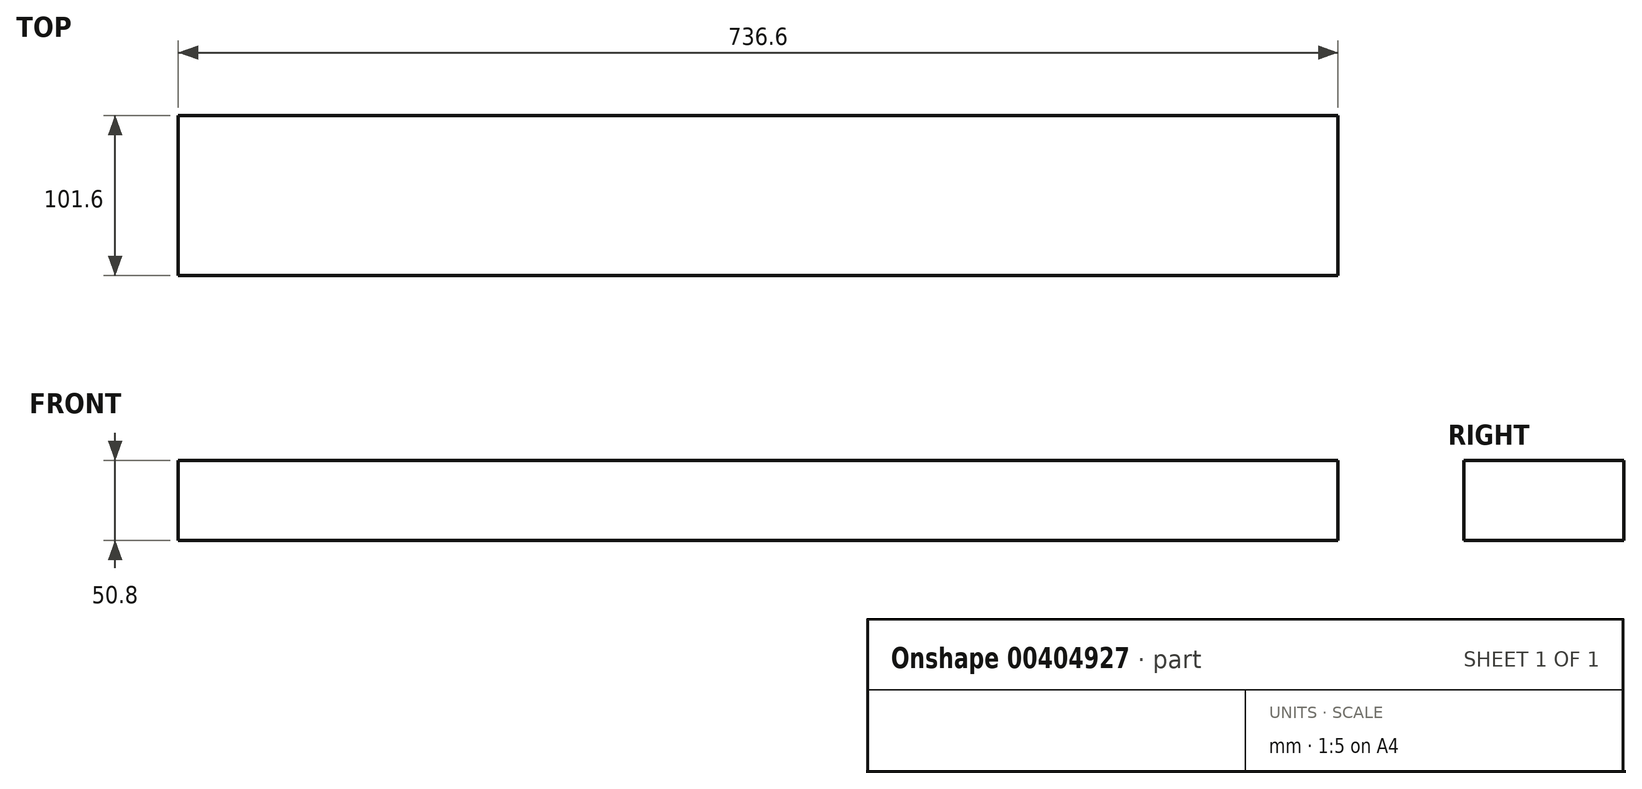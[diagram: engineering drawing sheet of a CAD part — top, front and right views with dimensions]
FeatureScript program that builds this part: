
annotation { "Feature Type Name" : "Feature", "Feature Type Description" : "" }
export const myFeature = defineFeature(function(context is Context, id is Id, definition is map)
    precondition{}
    {
        {
            var Q0;
            Q0=qCreatedBy(makeId("Right.planeOp"),FACE);
            var sketch = newSketch(context, id + "F0", { "sketchPlane" : qUnion([Q0])});
            skLineSegment(sketch, "E0.bottom", {"start": v(0, 0) * mm, "end": v(101.6, 0) * mm});
            skLineSegment(sketch, "E0.top", {"start": v(0, 50.8) * mm, "end": v(101.6, 50.8) * mm});
            skLineSegment(sketch, "E0.left", {"start": v(0, 0) * mm, "end": v(0, 50.8) * mm});
            skLineSegment(sketch, "E0.right", {"start": v(101.6, 0) * mm, "end": v(101.6, 50.8) * mm});
            skSolve(sketch);
        }
        {
            var Q0;
            Q0=qSketchRegion(id+"F0",true);
            extrude(context, id + "F1", {"entities" : qUnion([Q0]), "depth" : 736.6 * mm});
        }
    });
